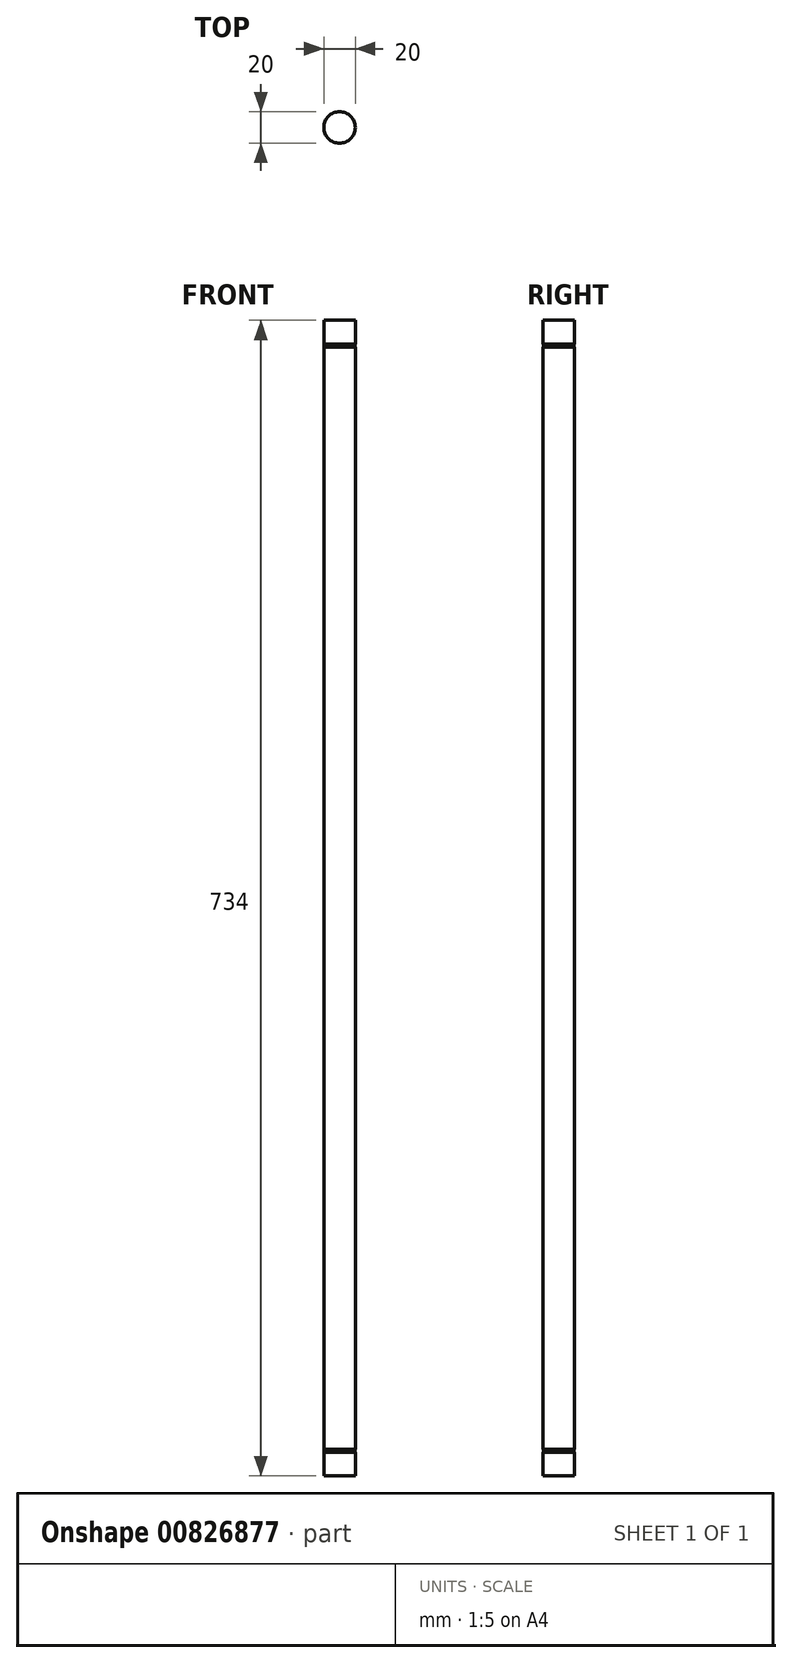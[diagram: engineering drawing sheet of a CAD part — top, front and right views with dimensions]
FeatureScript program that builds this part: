
annotation { "Feature Type Name" : "Feature", "Feature Type Description" : "" }
export const myFeature = defineFeature(function(context is Context, id is Id, definition is map)
    precondition{}
    {
        {
            var Q0;
            Q0=qCreatedBy(makeId("Top.planeOp"),FACE);
            var sketch = newSketch(context, id + "F0", { "sketchPlane" : qUnion([Q0])});
            skCircle(sketch, "E0", {"center": v(0, 0) * mm, "radius": 10 * mm});
            skSolve(sketch);
        }
        {
            var Q0;
            Q0=makeQuery(id+"F0.imprint","IMPRINT",FACE,{"disambiguationData":[TD([[makeQuery(id+"F0.imprint","IMPRINT",EDGE,{"derivedFrom":sQuery(id+"F0.wireOp",EDGE,"E0")}),1.0]])]});
            extrude(context, id + "F1", {"entities" : qUnion([Q0]), "depth" : 700 * mm, "offsetDistance" : 25 * mm});
        }
        {
            var Q0;
            Q0=makeQuery(id+"F1.opExtrude","CAP_FACE",FACE,{"disambiguationData":[OSD([sQuery(id+"F0.wireOp",EDGE,"E0")])],"isStart":true});
            var sketch = newSketch(context, id + "F2", { "sketchPlane" : qUnion([Q0])});
            skCircle(sketch, "E1", {"center": v(0, 0) * mm, "radius": 9.75 * mm});
            skSolve(sketch);
        }
        {
            var Q0;
            Q0=makeQuery(id+"F2.imprint","IMPRINT",FACE,{"disambiguationData":[TD([[makeQuery(id+"F2.imprint","IMPRINT",EDGE,{"derivedFrom":sQuery(id+"F2.wireOp",EDGE,"E1")}),1.0]])]});
            extrude(context, id + "F3", {"entities" : qUnion([Q0]), "operationType" : NewBodyOperationType.ADD, "depth" : 2 * mm, "offsetDistance" : 25 * mm});
        }
        {
            var Q0;
            Q0=makeQuery(id+"F3.opExtrude","CAP_FACE",FACE,{"disambiguationData":[OSD([sQuery(id+"F2.wireOp",EDGE,"E1")])],"isStart":false});
            var sketch = newSketch(context, id + "F4", { "sketchPlane" : qUnion([Q0])});
            skCircle(sketch, "E2", {"center": v(0, 0) * mm, "radius": 10 * mm});
            skSolve(sketch);
        }
        {
            var Q0;
            Q0=makeQuery(id+"F4.imprint","IMPRINT",FACE,{"disambiguationData":[TD([[makeQuery(id+"F4.imprint","IMPRINT",EDGE,{"derivedFrom":makeQuery(id+"F3.opExtrude","CAP_EDGE",EDGE,{"disambiguationData":[OSD([sQuery(id+"F2.wireOp",EDGE,"E1")])],"isStart":false})}),1.0]])]});
            var Q1;
            Q1=makeQuery(id+"F4.imprint","IMPRINT",FACE,{"disambiguationData":[TD([[makeQuery(id+"F4.imprint","IMPRINT",EDGE,{"derivedFrom":sQuery(id+"F4.wireOp",EDGE,"E2")}),1.0]])]});
            extrude(context, id + "F5", {"entities" : qUnion([Q0, Q1]), "operationType" : NewBodyOperationType.ADD, "depth" : 15 * mm, "offsetDistance" : 25 * mm});
        }
        {
            var Q0;
            Q0=makeQuery(id+"F1.opExtrude","CAP_FACE",FACE,{"disambiguationData":[OSD([sQuery(id+"F0.wireOp",EDGE,"E0")])],"isStart":false});
            var sketch = newSketch(context, id + "F6", { "sketchPlane" : qUnion([Q0])});
            skCircle(sketch, "E3", {"center": v(0, 0) * mm, "radius": 9.75 * mm});
            skSolve(sketch);
        }
        {
            var Q0;
            Q0=makeQuery(id+"F6.imprint","IMPRINT",FACE,{"disambiguationData":[TD([[makeQuery(id+"F6.imprint","IMPRINT",EDGE,{"derivedFrom":sQuery(id+"F6.wireOp",EDGE,"E3")}),1.0]])]});
            extrude(context, id + "F7", {"entities" : qUnion([Q0]), "operationType" : NewBodyOperationType.ADD, "depth" : 2 * mm, "offsetDistance" : 25 * mm});
        }
        {
            var Q0;
            Q0=makeQuery(id+"F7.opExtrude","CAP_FACE",FACE,{"disambiguationData":[OSD([sQuery(id+"F6.wireOp",EDGE,"E3")])],"isStart":false});
            var sketch = newSketch(context, id + "F8", { "sketchPlane" : qUnion([Q0])});
            skCircle(sketch, "E4", {"center": v(0, 0) * mm, "radius": 10 * mm});
            skSolve(sketch);
        }
        {
            var Q0;
            Q0=makeQuery(id+"F8.imprint","IMPRINT",FACE,{"disambiguationData":[TD([[makeQuery(id+"F8.imprint","IMPRINT",EDGE,{"derivedFrom":sQuery(id+"F8.wireOp",EDGE,"E4")}),1.0]])]});
            var Q1;
            Q1=makeQuery(id+"F8.imprint","IMPRINT",FACE,{"disambiguationData":[TD([[makeQuery(id+"F8.imprint","IMPRINT",EDGE,{"derivedFrom":makeQuery(id+"F7.opExtrude","CAP_EDGE",EDGE,{"disambiguationData":[OSD([sQuery(id+"F6.wireOp",EDGE,"E3")])],"isStart":false})}),1.0]])]});
            extrude(context, id + "F9", {"entities" : qUnion([Q0, Q1]), "operationType" : NewBodyOperationType.ADD, "depth" : 15 * mm, "offsetDistance" : 25 * mm});
        }
    });
